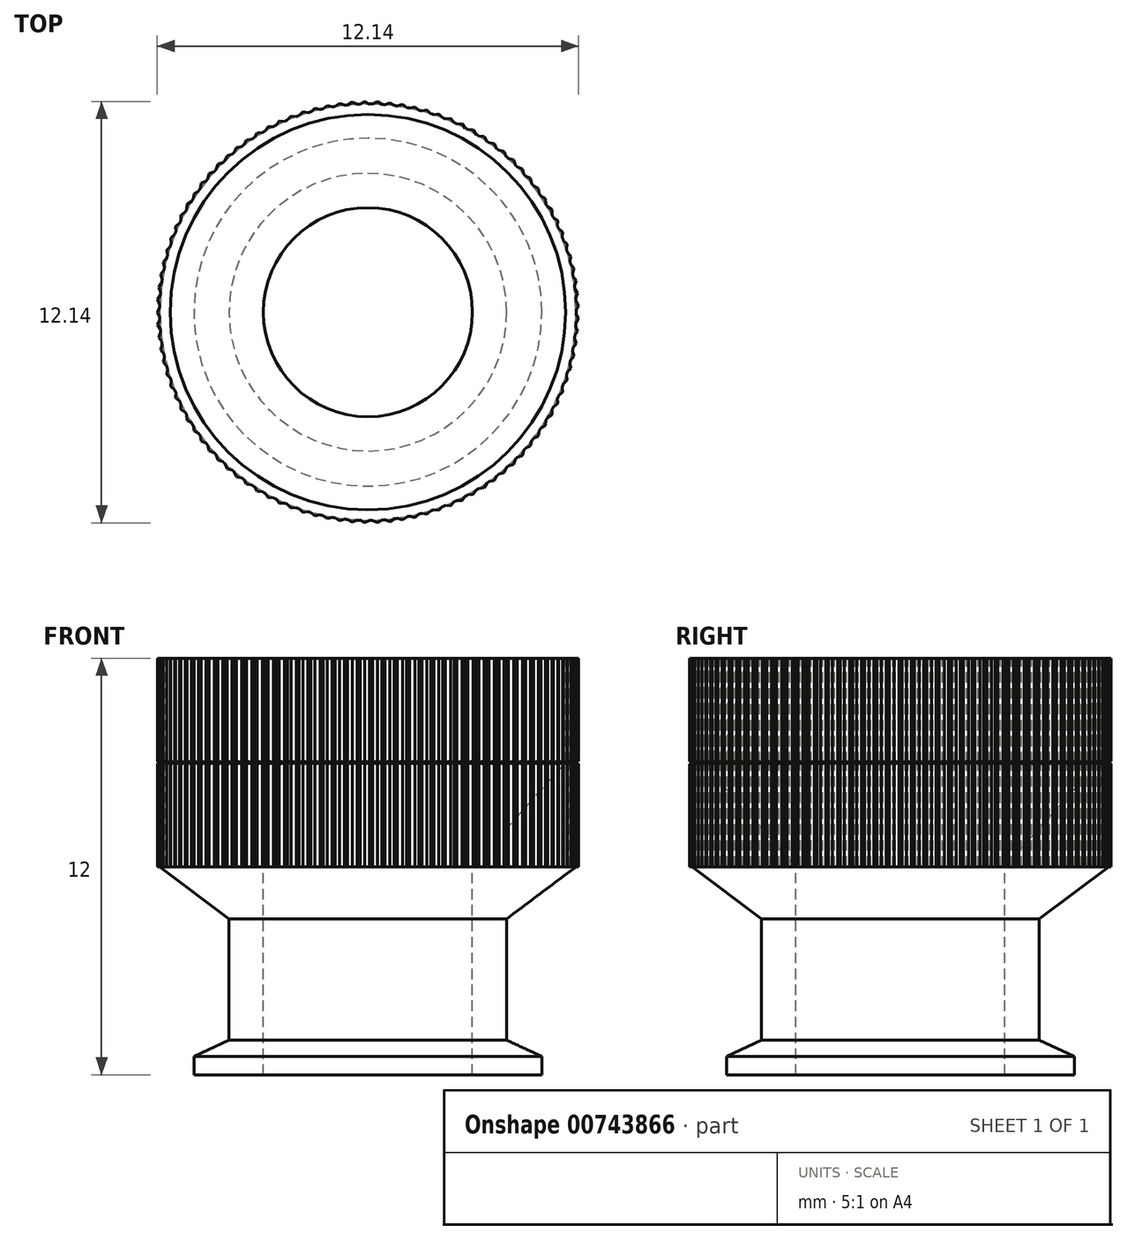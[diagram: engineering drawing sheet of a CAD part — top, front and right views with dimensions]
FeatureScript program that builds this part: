
annotation { "Feature Type Name" : "Feature", "Feature Type Description" : "" }
export const myFeature = defineFeature(function(context is Context, id is Id, definition is map)
    precondition{}
    {
        {
            var Q0;
            Q0=qCreatedBy(makeId("Right.planeOp"),FACE);
            var sketch = newSketch(context, id + "F0", { "sketchPlane" : qUnion([Q0])});
            skCircle(sketch, "E0", {"center": v(0, 0) * mm, "radius": 6 * mm});
            skSolve(sketch);
        }
        {
            var Q0;
            Q0=makeQuery(id+"F0.imprint","IMPRINT",FACE,{"disambiguationData":[TD([[makeQuery(id+"F0.imprint","IMPRINT",EDGE,{"derivedFrom":sQuery(id+"F0.wireOp",EDGE,"E0")}),1.0]])]});
            extrude(context, id + "F1", {"entities" : qUnion([Q0]), "depth" : 6 * mm, "offsetDistance" : 25 * mm});
        }
        {
            var Q0;
            Q0=makeQuery(id+"F1.opExtrude","CAP_FACE",FACE,{"disambiguationData":[OSD([sQuery(id+"F0.wireOp",EDGE,"E0")])],"isStart":false});
            var sketch = newSketch(context, id + "F2", { "sketchPlane" : qUnion([Q0])});
            skCircle(sketch, "E1", {"center": v(0, 0) * mm, "radius": 5.6 * mm});
            skSolve(sketch);
        }
        {
            var Q0;
            Q0=makeQuery(id+"F2.imprint","IMPRINT",FACE,{"disambiguationData":[TD([[makeQuery(id+"F2.imprint","IMPRINT",EDGE,{"derivedFrom":sQuery(id+"F2.wireOp",EDGE,"E1")}),1.0]])]});
            extrude(context, id + "F3", {"entities" : qUnion([Q0]), "operationType" : NewBodyOperationType.REMOVE, "oppositeDirection" : true, "depth" : 3 * mm, "offsetDistance" : 25 * mm});
        }
        {
            var Q0;
            Q0=makeQuery(id+"F1.opExtrude","SWEPT_BODY",BODY,{"disambiguationData":[OSD([sQuery(id+"F0.wireOp",EDGE,"E0")])]});
            deleteBodies(context, id + "F4", {"entities" : qUnion([Q0])});
        }
        {
            var Q0;
            Q0=qCreatedBy(makeId("Right.planeOp"),FACE);
            var sketch = newSketch(context, id + "F5", { "sketchPlane" : qUnion([Q0])});
            skLineSegment(sketch, "E2", {"start": v(0, 11.22) * mm, "end": v(0, 0) * mm, "construction": true});
            skLineSegment(sketch, "E3", {"start": v(6, 10.3) * mm, "end": v(6, 4.3) * mm});
            skLineSegment(sketch, "E4", {"start": v(4, 2.8) * mm, "end": v(4, -0.7) * mm});
            skLineSegment(sketch, "E5", {"start": v(4, 2.8) * mm, "end": v(6, 4.3) * mm});
            skLineSegment(sketch, "E6", {"start": v(5.01, -1.49) * mm, "end": v(5.01, -1.7) * mm});
            skLineSegment(sketch, "E7", {"start": v(4, -0.7) * mm, "end": v(5.01, -1.16) * mm});
            skLineSegment(sketch, "E8", {"start": v(5.01, -1.49) * mm, "end": v(5.01, -1.16) * mm});
            skLineSegment(sketch, "E9", {"start": v(5.01, -1.7) * mm, "end": v(3.01, -1.7) * mm});
            skLineSegment(sketch, "E10", {"start": v(3.01, -1.7) * mm, "end": v(3.01, 2.8) * mm});
            skLineSegment(sketch, "E11", {"start": v(3.01, 2.8) * mm, "end": v(3.01, 4.3) * mm});
            skLineSegment(sketch, "E12", {"start": v(3.01, 4.3) * mm, "end": v(5.7, 7.3) * mm});
            skPoint(sketch, "E12.endSnap0", {"position": v(6, 7.3) * mm});
            skLineSegment(sketch, "E13", {"start": v(5.7, 7.3) * mm, "end": v(5.7, 10.3) * mm});
            skLineSegment(sketch, "E14", {"start": v(5.7, 10.3) * mm, "end": v(6, 10.3) * mm});
            skSolve(sketch);
        }
        {
            var Q0;
            Q0=makeQuery(id+"F5.imprint","IMPRINT",FACE,{"disambiguationData":[TD([[makeQuery(id+"F5.imprint","IMPRINT",EDGE,{"derivedFrom":sQuery(id+"F5.wireOp",EDGE,"E3")}),-1.0]])]});
            var Q1;
            Q1=sQuery(id+"F5.wireOp",EDGE,"E2");
            revolve(context, id + "F6", {"surfaceOperationType" : NewSurfaceOperationType.NEW, "entities" : qUnion([Q0]), "axis" : qUnion([Q1]), "revolveType" : RevolveType.FULL});
        }
        {
            var Q0;
            Q0=qCreatedBy(makeId("Right.planeOp"),FACE);
            var sketch = newSketch(context, id + "F7", { "sketchPlane" : qUnion([Q0])});
            skLineSegment(sketch, "E15.bottom", {"start": v(26.77, 11.19) * mm, "end": v(16, 11.19) * mm});
            skLineSegment(sketch, "E15.top", {"start": v(26.77, -2.4) * mm, "end": v(16, -2.4) * mm});
            skLineSegment(sketch, "E15.left", {"start": v(26.77, 11.19) * mm, "end": v(26.77, -2.4) * mm});
            skLineSegment(sketch, "E15.right", {"start": v(16, 11.19) * mm, "end": v(16, -2.4) * mm});
            skSolve(sketch);
        }
        {
            var Q0;
            Q0=makeQuery(id+"F6.opRevolve","SWEPT_FACE",FACE,{"disambiguationData":[OSD([sQuery(id+"F5.wireOp",EDGE,"E14")])]});
            cPlane(context, id + "F8", {"entities" : qUnion([Q0]), "cplaneType" : CPlaneType.OFFSET, "offset" : 25 * mm, "width" : 150 * mm, "height" : 150 * mm});
        }
        {
            var Q0;
            Q0=qCreatedBy(id+"F8.planeOp",FACE);
            var sketch = newSketch(context, id + "F9", { "sketchPlane" : qUnion([Q0])});
            skLineSegment(sketch, "E16", {"start": v(-6, 0.15) * mm, "end": v(-6.07, 0) * mm});
            skLineSegment(sketch, "E17", {"start": v(-6.07, 0) * mm, "end": v(-6, -0.15) * mm});
            skLineSegment(sketch, "E18", {"start": v(-6, 0.15) * mm, "end": v(-6, -0.15) * mm});
            skSolve(sketch);
        }
        {
            var Q0;
            Q0=makeQuery(id+"F9.imprint","IMPRINT",FACE,{"disambiguationData":[TD([[makeQuery(id+"F9.imprint","IMPRINT",EDGE,{"derivedFrom":sQuery(id+"F9.wireOp",EDGE,"E16")}),1.0]])]});
            extrude(context, id + "F10", {"entities" : qUnion([Q0]), "oppositeDirection" : true, "depth" : 31 * mm, "offsetDistance" : 25 * mm});
        }
        {
            var Q0;
            Q0=makeQuery(id+"F10.opExtrude","CAP_FACE",FACE,{"disambiguationData":[OSD([sQuery(id+"F9.wireOp",EDGE,"E16"),sQuery(id+"F9.wireOp",EDGE,"E17"),sQuery(id+"F9.wireOp",EDGE,"E18")])],"isStart":true});
            extrude(context, id + "F11", {"entities" : qUnion([Q0]), "operationType" : NewBodyOperationType.REMOVE, "oppositeDirection" : true, "depth" : 25 * mm, "offsetDistance" : 25 * mm});
        }
        {
            var Q0;
            Q0=makeQuery(id+"F10.opExtrude","SWEPT_BODY",BODY,{"disambiguationData":[OSD([sQuery(id+"F9.wireOp",EDGE,"E16"),sQuery(id+"F9.wireOp",EDGE,"E17"),sQuery(id+"F9.wireOp",EDGE,"E18")])]});
            var Q1;
            Q1=makeQuery(id+"F6.opRevolve","SWEPT_FACE",FACE,{"disambiguationData":[OSD([sQuery(id+"F5.wireOp",EDGE,"E3")])]});
            circularPattern(context, id + "F12", {"operationType" : NewBodyOperationType.ADD, "entities" : qUnion([Q0]), "axis" : qUnion([Q1]), "angle" : 360 * degree, "instanceCount" : 105, "oppositeDirection" : true, "equalSpace" : true});
        }
        {
            var Q0;
            Q0=qCreatedBy(makeId("Front.planeOp"),FACE);
            var sketch = newSketch(context, id + "F13", { "sketchPlane" : qUnion([Q0])});
            skLineSegment(sketch, "E19", {"start": v(0, 11.66) * mm, "end": v(0, 1.93) * mm, "construction": true});
            skLineSegment(sketch, "E20", {"start": v(6, 7.3) * mm, "end": v(6.1, 7.36) * mm});
            skLineSegment(sketch, "E21", {"start": v(6.1, 7.36) * mm, "end": v(6.1, 7.25) * mm});
            skLineSegment(sketch, "E22", {"start": v(6.1, 7.25) * mm, "end": v(6, 7.3) * mm});
            skSolve(sketch);
        }
        {
            var Q0;
            Q0=makeQuery(id+"F13.imprint","IMPRINT",FACE,{"disambiguationData":[TD([[makeQuery(id+"F13.imprint","IMPRINT",EDGE,{"derivedFrom":sQuery(id+"F13.wireOp",EDGE,"E20")}),-1.0]])]});
            var Q1;
            Q1=sQuery(id+"F13.wireOp",EDGE,"E19");
            revolve(context, id + "F14", {"operationType" : NewBodyOperationType.REMOVE, "surfaceOperationType" : NewSurfaceOperationType.NEW, "entities" : qUnion([Q0]), "axis" : qUnion([Q1]), "revolveType" : RevolveType.FULL, "oppositeDirection" : true});
        }
    });
